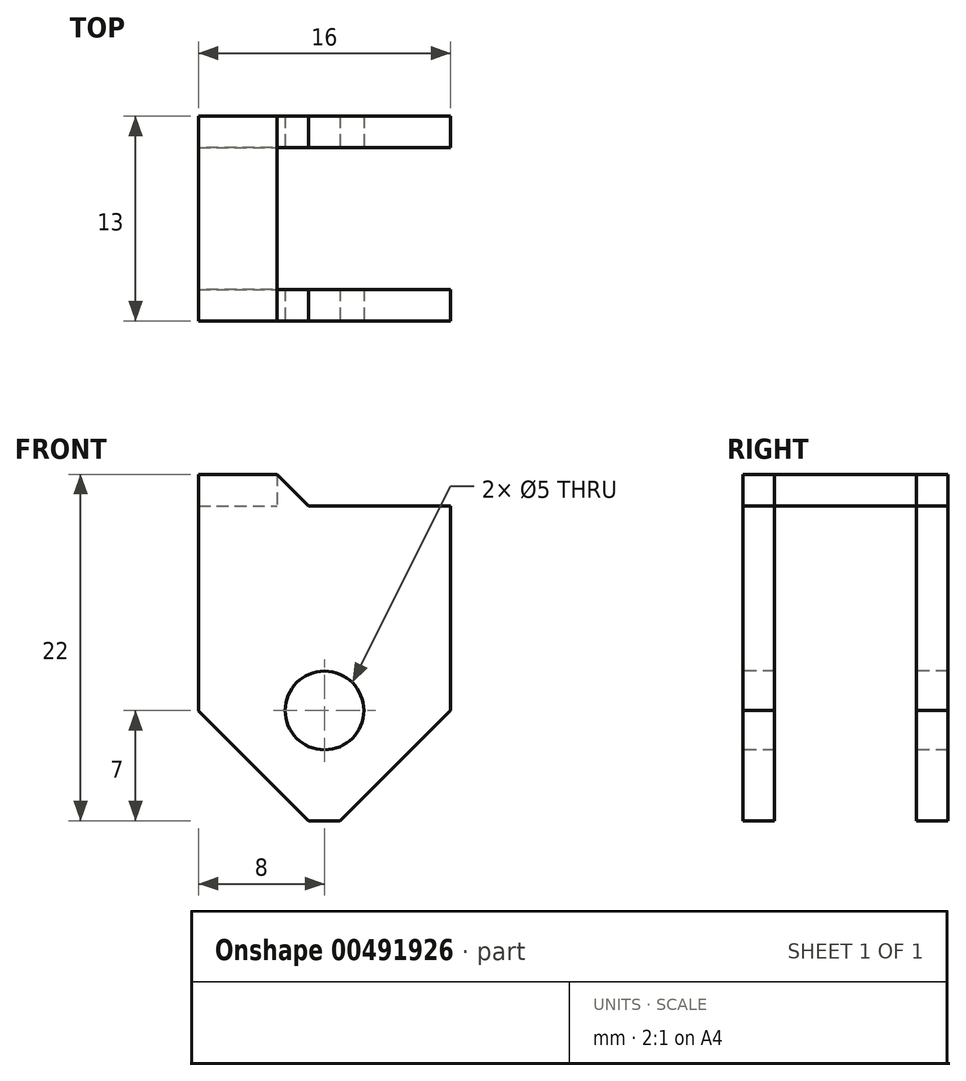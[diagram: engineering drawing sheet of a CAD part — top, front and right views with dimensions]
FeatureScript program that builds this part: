
annotation { "Feature Type Name" : "Feature", "Feature Type Description" : "" }
export const myFeature = defineFeature(function(context is Context, id is Id, definition is map)
    precondition{}
    {
        {
            var Q0;
            Q0=qCreatedBy(makeId("Front.planeOp"),FACE);
            var sketch = newSketch(context, id + "F0", { "sketchPlane" : qUnion([Q0])});
            skLineSegment(sketch, "E0.bottom", {"start": v(-16, 11) * mm, "end": v(16, 11) * mm});
            skLineSegment(sketch, "E0.top", {"start": v(-16, -11) * mm, "end": v(16, -11) * mm});
            skLineSegment(sketch, "E0.left", {"start": v(-16, 11) * mm, "end": v(-16, -11) * mm});
            skLineSegment(sketch, "E0.right", {"start": v(16, 11) * mm, "end": v(16, -11) * mm});
            skPoint(sketch, "E0.middle", {"position": v(0, 0) * mm});
            skSolve(sketch);
        }
        {
            assignVariable(context, id + "F1", {"name" : "depth", "anyValue" : 13});
        }
        {
            var Q0;
            Q0=makeQuery(id+"F0.imprint","IMPRINT",FACE,{"disambiguationData":[TD([[makeQuery(id+"F0.imprint","IMPRINT",EDGE,{"derivedFrom":sQuery(id+"F0.wireOp",EDGE,"E0.bottom")}),-1.0]])]});
            extrude(context, id + "F2", {"entities" : qUnion([Q0]), "depth" : (getVariable(context, 'depth')) * mm});
        }
        {
            var Q0;
            Q0=makeQuery(id+"F2.opExtrude","SWEPT_EDGE",EDGE,{"disambiguationData":[OSD([sQuery(id+"F0.wireOp",EDGE,"E0.top"),sQuery(id+"F0.wireOp",EDGE,"E0.left")])]});
            var Q1;
            Q1=makeQuery(id+"F2.opExtrude","SWEPT_EDGE",EDGE,{"disambiguationData":[OSD([sQuery(id+"F0.wireOp",EDGE,"E0.top"),sQuery(id+"F0.wireOp",EDGE,"E0.right")])]});
            chamfer(context, id + "F3", {"entities" : qUnion([Q0, Q1]), "width" : 7 * mm, "tangentPropagation" : true});
        }
        {
            var Q0;
            Q0=makeQuery(id+"F2.opExtrude","CAP_FACE",FACE,{"disambiguationData":[OSD([sQuery(id+"F0.wireOp",EDGE,"E0.bottom"),sQuery(id+"F0.wireOp",EDGE,"E0.top"),sQuery(id+"F0.wireOp",EDGE,"E0.left"),sQuery(id+"F0.wireOp",EDGE,"E0.right")])],"isStart":false});
            var sketch = newSketch(context, id + "F4", { "sketchPlane" : qUnion([Q0])});
            skCircle(sketch, "E1", {"center": v(-8, -4) * mm, "radius": 2.5 * mm});
            skCircle(sketch, "E2", {"center": v(8, -4) * mm, "radius": 2.5 * mm});
            skSolve(sketch);
        }
        {
            var Q0;
            Q0=makeQuery(id+"F4.imprint","IMPRINT",FACE,{"disambiguationData":[TD([[makeQuery(id+"F4.imprint","IMPRINT",EDGE,{"derivedFrom":sQuery(id+"F4.wireOp",EDGE,"E1")}),1.0]])]});
            var Q1;
            Q1=makeQuery(id+"F4.imprint","IMPRINT",FACE,{"disambiguationData":[TD([[makeQuery(id+"F4.imprint","IMPRINT",EDGE,{"derivedFrom":sQuery(id+"F4.wireOp",EDGE,"E2")}),1.0]])]});
            extrude(context, id + "F5", {"entities" : qUnion([Q0, Q1]), "operationType" : NewBodyOperationType.REMOVE, "oppositeDirection" : true, "depth" : 25 * mm});
        }
        {
            var Q0;
            Q0=makeQuery(id+"F2.opExtrude","SWEPT_FACE",FACE,{"disambiguationData":[OSD([sQuery(id+"F0.wireOp",EDGE,"E0.top")])]});
            var Q1;
            Q1=makeQuery(id+"F3.opChamfer","BLEND_FACE",FACE,{"disambiguationData":[OSD([sQuery(id+"F0.wireOp",EDGE,"E0.top"),sQuery(id+"F0.wireOp",EDGE,"E0.right")])]});
            var Q2;
            Q2=makeQuery(id+"F2.opExtrude","SWEPT_FACE",FACE,{"disambiguationData":[OSD([sQuery(id+"F0.wireOp",EDGE,"E0.right")])]});
            var Q3;
            Q3=makeQuery(id+"F2.opExtrude","SWEPT_FACE",FACE,{"disambiguationData":[OSD([sQuery(id+"F0.wireOp",EDGE,"E0.left")])]});
            var Q4;
            Q4=makeQuery(id+"F3.opChamfer","BLEND_FACE",FACE,{"disambiguationData":[OSD([sQuery(id+"F0.wireOp",EDGE,"E0.top"),sQuery(id+"F0.wireOp",EDGE,"E0.left")])]});
            var Q5;
            Q5=makeQuery(id+"F5.boolean.opBoolean","COPY",FACE,{"derivedFrom":makeQuery(id+"F5.opExtrude","SWEPT_FACE",FACE,{"disambiguationData":[OSD([sQuery(id+"F4.wireOp",EDGE,"E1")])]})});
            var Q6;
            Q6=makeQuery(id+"F5.boolean.opBoolean","COPY",FACE,{"derivedFrom":makeQuery(id+"F5.opExtrude","SWEPT_FACE",FACE,{"disambiguationData":[OSD([sQuery(id+"F4.wireOp",EDGE,"E2")])]})});
            shell(context, id + "F6", {"entities" : qUnion([Q0, Q1, Q2, Q3, Q4, Q5, Q6]), "thickness" : 2 * mm});
        }
        {
            var Q0;
            Q0=makeQuery(id+"F2.opExtrude","SWEPT_FACE",FACE,{"disambiguationData":[OSD([sQuery(id+"F0.wireOp",EDGE,"E0.bottom")])]});
            var sketch = newSketch(context, id + "F7", { "sketchPlane" : qUnion([Q0])});
            skLineSegment(sketch, "E3.bottom", {"start": v(16, -13) * mm, "end": v(5, -13) * mm});
            skLineSegment(sketch, "E3.top", {"start": v(16, 0) * mm, "end": v(5, 0) * mm});
            skLineSegment(sketch, "E3.left", {"start": v(16, -13) * mm, "end": v(16, 0) * mm});
            skLineSegment(sketch, "E3.right", {"start": v(5, -13) * mm, "end": v(5, 0) * mm});
            skLineSegment(sketch, "E4.bottom", {"start": v(-16, -13) * mm, "end": v(-5, -13) * mm});
            skLineSegment(sketch, "E4.top", {"start": v(-16, 0) * mm, "end": v(-5, 0) * mm});
            skLineSegment(sketch, "E4.left", {"start": v(-16, -13) * mm, "end": v(-16, 0) * mm});
            skLineSegment(sketch, "E4.right", {"start": v(-5, -13) * mm, "end": v(-5, 0) * mm});
            skSolve(sketch);
        }
        {
            var Q0;
            Q0=makeQuery(id+"F7.imprint","IMPRINT",FACE,{"disambiguationData":[TD([[makeQuery(id+"F7.imprint","IMPRINT",EDGE,{"derivedFrom":sQuery(id+"F7.wireOp",EDGE,"E3.bottom")}),1.0]])]});
            var Q1;
            Q1=makeQuery(id+"F7.imprint","IMPRINT",FACE,{"disambiguationData":[TD([[makeQuery(id+"F7.imprint","IMPRINT",EDGE,{"derivedFrom":sQuery(id+"F7.wireOp",EDGE,"E4.bottom")}),1.0]])]});
            extrude(context, id + "F8", {"entities" : qUnion([Q0, Q1]), "operationType" : NewBodyOperationType.REMOVE, "oppositeDirection" : true, "depth" : 2 * mm});
        }
        {
            var Q0;
            {var subQ0=sQuery(id+"F7.wireOp",EDGE,"E3.right");Q0=makeQuery(id+"F8.boolean.opBoolean","COPY",EDGE,{"disambiguationData":[topologyDisambiguationEdgeConnected([makeQuery(id+"F6.opShell","OFFSET_FACE",FACE,{"disambiguationData":[OSD([sQuery(id+"F0.wireOp",EDGE,"E0.bottom")])]}),makeQuery(id+"F8.opExtrude","SWEPT_FACE",FACE,{"disambiguationData":[OSD([subQ0])]})])],"derivedFrom":makeQuery(id+"F8.opExtrude","CAP_EDGE",EDGE,{"disambiguationData":[OSD([subQ0])],"isStart":false})});}
            var Q1;
            {var subQ0=sQuery(id+"F7.wireOp",EDGE,"E4.right");Q1=makeQuery(id+"F8.boolean.opBoolean","COPY",EDGE,{"disambiguationData":[topologyDisambiguationEdgeConnected([makeQuery(id+"F6.opShell","OFFSET_FACE",FACE,{"disambiguationData":[OSD([sQuery(id+"F0.wireOp",EDGE,"E0.bottom")])]}),makeQuery(id+"F8.opExtrude","SWEPT_FACE",FACE,{"disambiguationData":[OSD([subQ0])]})])],"derivedFrom":makeQuery(id+"F8.opExtrude","CAP_EDGE",EDGE,{"disambiguationData":[OSD([subQ0])],"isStart":false})});}
            chamfer(context, id + "F9", {"entities" : qUnion([Q0, Q1]), "width" : 2 * mm, "tangentPropagation" : true});
        }
        {
            var Q0;
            Q0=makeQuery(id+"F2.opExtrude","CAP_FACE",FACE,{"disambiguationData":[OSD([sQuery(id+"F0.wireOp",EDGE,"E0.bottom"),sQuery(id+"F0.wireOp",EDGE,"E0.top"),sQuery(id+"F0.wireOp",EDGE,"E0.left"),sQuery(id+"F0.wireOp",EDGE,"E0.right")])],"isStart":true});
            var sketch = newSketch(context, id + "F10", { "sketchPlane" : qUnion([Q0])});
            skLineSegment(sketch, "E5", {"start": v(0, -4.01) * mm, "end": v(-7, -11) * mm});
            skLineSegment(sketch, "E6", {"start": v(-7, -11) * mm, "end": v(7, -11) * mm});
            skLineSegment(sketch, "E7", {"start": v(7, -11) * mm, "end": v(0, -4.01) * mm});
            skSolve(sketch);
        }
        {
            var Q0;
            Q0=makeQuery(id+"F10.imprint","IMPRINT",FACE,{"disambiguationData":[TD([[makeQuery(id+"F10.imprint","IMPRINT",EDGE,{"derivedFrom":sQuery(id+"F10.wireOp",EDGE,"E5")}),1.0]])]});
            extrude(context, id + "F11", {"entities" : qUnion([Q0]), "operationType" : NewBodyOperationType.REMOVE, "oppositeDirection" : true, "depth" : 25 * mm});
        }
        {
            var Q0;
            Q0=makeQuery(id+"F2.opExtrude","CAP_FACE",FACE,{"disambiguationData":[OSD([sQuery(id+"F0.wireOp",EDGE,"E0.bottom"),sQuery(id+"F0.wireOp",EDGE,"E0.top"),sQuery(id+"F0.wireOp",EDGE,"E0.left"),sQuery(id+"F0.wireOp",EDGE,"E0.right")])],"isStart":false});
            var sketch = newSketch(context, id + "F12", { "sketchPlane" : qUnion([Q0])});
            skLineSegment(sketch, "E8", {"start": v(0, 11) * mm, "end": v(0, -4.01) * mm});
            skSolve(sketch);
        }
        {
            var Q0;
            {var subQ7=sQuery(id+"F12.wireOp",EDGE,"E8");Q0=makeQuery(id+"F12.imprint","IMPRINT",FACE,{"disambiguationData":[TD([[makeQuery(id+"F12.imprint","IMPRINT",EDGE,{"derivedFrom":subQ7}),-1.0]])]});}
            extrude(context, id + "F13", {"entities" : qUnion([Q0]), "operationType" : NewBodyOperationType.REMOVE, "oppositeDirection" : true, "depth" : 25 * mm});
        }
    });
